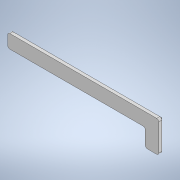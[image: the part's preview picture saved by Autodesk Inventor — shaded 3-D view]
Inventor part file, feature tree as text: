
AUTODESK INVENTOR PART (.ipt)
format: ipt  version: 2022 (Build 260153000, 153)  size: 137,728 bytes
history: native  units: mm
features: extrude x3, sketch x2, fillet x1, projected_geometry x1
ambient origin geometry x8: Origin, YZ Plane, XZ Plane, XY Plane, X Axis, Y Axis, Z Axis, Center Point
bodies: Solid1 (feature_tree)
feature tree (7):
  sketch  "Sketch1"  dims[d0=132.5mm d1=10.0mm]
  extrude  "Extrusion1"  Depth=10.0mm
  extrude  "Extrusion2"  Depth=20.0mm
  extrude  "Extrusion3"  Depth=3.0mm
  fillet  "Fillet2"  Radius=3.0mm
  sketch  "Sketch2"  dims[d2=10.0mm d3=20.0mm d4=3.0mm d5=3.0mm d6=3.0mm d7=0.0mm d8=10.0mm d9=0.0mm d11=3.0mm d12=0.0mm d13=2.0mm]
  projected_geometry  "Projected Loop1"
